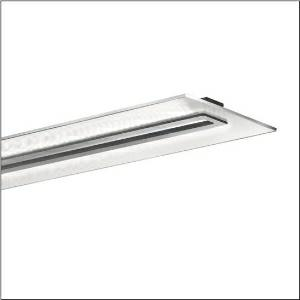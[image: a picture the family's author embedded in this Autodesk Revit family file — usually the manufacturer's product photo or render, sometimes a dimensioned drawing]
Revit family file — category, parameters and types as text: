
# Revit family: vega_11_5mn238dle0s
name_source: partatom
category: Lighting Fixtures
units: mm (PartAtom-declared; Revit-internal decimal feet)

## family parameters
Cut with Voids When Loaded = No
Host = Face
Light Source = No
Part Type = Normal
Room Calculation Point = No
Round Connector Dimension = Use Diameter
Shared = No

## types (1)
- --- (1 x LED 4000K / CRI = 80 (unbekannt), 8130 lm, 4000K)
    Apparent Load = 62 VA
    CIE Flux Codes = 61 86 97 62 100
    Color Rendering = 80
    Color Temperature = 4000K
    Default Elevation = 1800 mm
    Description = Vega 11, office luminaire, primary light control with prismatic reflector, of PMMA, transparent prismatic structure, CAT 2 (L<= 1500cd/m²), light emission: direct/indirect distribution, primary light characteristic: symmetric, installation type: suspended mounting, surface-mounted, LED, rated luminous flux: 8.130lm, luminous efficacy: 131lm/W, light colour: 840, colour temperature: 4000K, control gear: DALI, with terminal, 3+2-pole, max. 2.5mm², mains connection: 230V, AC, 50Hz, connection cable inclusive, cable length: 1,5m, rated input power: 62W, luminaire housing, rectangular, rounded, of aluminium section, anodised, metallic grey (RAL 9006), length: 1.250mm, width: 350mm, height: 43mm, luminaire housing, lower part, of aluminium section, anodised, metallic grey (RAL 9006), of PC, grey, protection rating (complete): IP20, insulation class (complete): insulation class I (protective earthing), certification: CE, permissible operating ambient temperature: 0..+35°C, standard: EN 50419, packaging unit: 1 piece
    Height = 40 mm  [stored 0.131234 ft]
    Lamp = 1 x LED 4000K / CRI >= 80 (unbekannt)
    Lamp Light Flux = 8130 lm
    Lamp count = 1
    Length = 1250 mm
    Luminous efficacy = 131 lm/W
    Manufacturer = Siteco
    ModVariant = No
    Model = 5MN238DLE0S
    Mounting Place = Ceiling
    Mounting Type = Pendant
    Number of Poles = 1
    OnlyDefault = Yes
    Power Factor = 1
    Product Name = Vega 11
    Product group = office luminaire | ceiling pendant
    ProductGroupID = 903
    Protection Class = Protection class I
    Protection Degree = IP 20
    RLX_Detail_Level = 1
    RLX_Emergency_Light_Flux = 0 lm
    RLX_Emergency_Type = 0
    RLX_Emergency_Type_DB = No
    RlxData = <blob elided: 62845 chars, md5=f7655898>
    Socket = socket
    Standby Power = 0 W
    System Light Flux = 8130 lm
    System Power = 62 W
    Type Comments = factory setting: luminous flux: 100 % | dim-lin: 254 | 458 mA
    Type Image = l_1004807.jpg
    URL = http://relux.com
    VarID = @adj_197103
    Voltage = 0 V
    Weight = 0.00 kg
    Width = 350 mm

note: [stored X ft] marks values corroborated as IEEE doubles in the binary element streams (Revit-internal decimal feet)

## geometry (parser evidence)
native form markers: Blend x4, Sweep x13
no freeform markers — native parametric forms only
